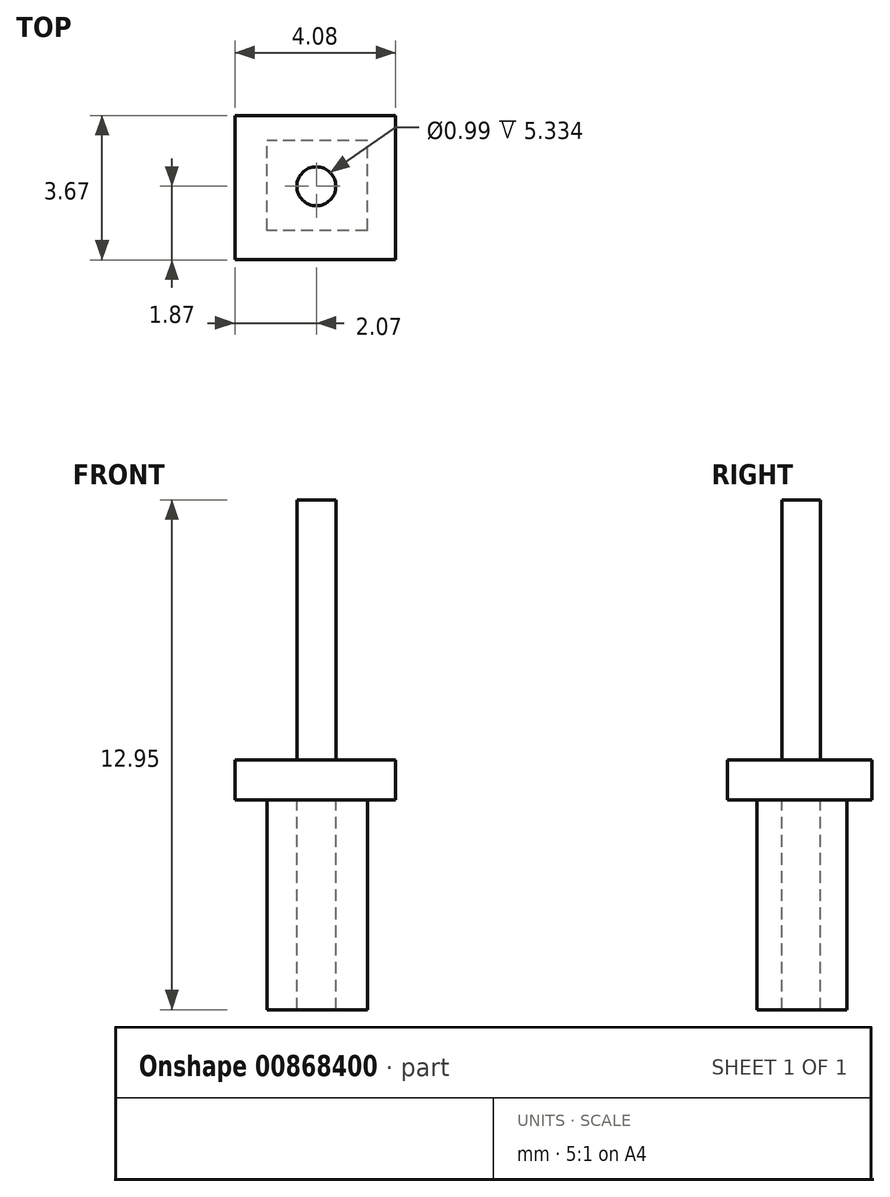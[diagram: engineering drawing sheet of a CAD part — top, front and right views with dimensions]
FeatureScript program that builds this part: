
annotation { "Feature Type Name" : "Feature", "Feature Type Description" : "" }
export const myFeature = defineFeature(function(context is Context, id is Id, definition is map)
    precondition{}
    {
        {
            var Q0;
            Q0=qCreatedBy(makeId("Top.planeOp"),FACE);
            var sketch = newSketch(context, id + "F0", { "sketchPlane" : qUnion([Q0])});
            skCircle(sketch, "E0", {"center": v(0, 0) * mm, "radius": 0.5 * mm});
            skLineSegment(sketch, "E1.bottom", {"start": v(-1.25, 1.16) * mm, "end": v(1.3, 1.16) * mm});
            skLineSegment(sketch, "E1.top", {"start": v(-1.25, -1.12) * mm, "end": v(1.3, -1.12) * mm});
            skLineSegment(sketch, "E1.left", {"start": v(-1.25, 1.16) * mm, "end": v(-1.25, -1.12) * mm});
            skLineSegment(sketch, "E1.right", {"start": v(1.3, 1.16) * mm, "end": v(1.3, -1.12) * mm});
            skSolve(sketch);
        }
        {
            var Q0;
            Q0=qCreatedBy(makeId("Top.planeOp"),FACE);
            var sketch = newSketch(context, id + "F1", { "sketchPlane" : qUnion([Q0])});
            skLineSegment(sketch, "E2.bottom", {"start": v(-2.07, 1.8) * mm, "end": v(2, 1.8) * mm});
            skLineSegment(sketch, "E2.top", {"start": v(-2.07, -1.87) * mm, "end": v(2, -1.87) * mm});
            skLineSegment(sketch, "E2.left", {"start": v(-2.07, 1.8) * mm, "end": v(-2.07, -1.87) * mm});
            skLineSegment(sketch, "E2.right", {"start": v(2, 1.8) * mm, "end": v(2, -1.87) * mm});
            skSolve(sketch);
        }
        {
            var Q0;
            Q0=makeQuery(id+"F0.imprint","IMPRINT",FACE,{"disambiguationData":[TD([[makeQuery(id+"F0.imprint","IMPRINT",EDGE,{"derivedFrom":sQuery(id+"F0.wireOp",EDGE,"E0")}),-1.0]])]});
            extrude(context, id + "F2", {"entities" : qUnion([Q0]), "oppositeDirection" : true, "depth" : 6.35 * mm, "offsetDistance" : 25.4 * mm});
        }
        {
            var Q0;
            Q0=makeQuery(id+"F1.imprint","IMPRINT",FACE,{"disambiguationData":[TD([[makeQuery(id+"F1.imprint","IMPRINT",EDGE,{"derivedFrom":sQuery(id+"F1.wireOp",EDGE,"E2.bottom")}),-1.0]])]});
            extrude(context, id + "F3", {"entities" : qUnion([Q0]), "operationType" : NewBodyOperationType.ADD, "oppositeDirection" : true, "depth" : 1.02 * mm, "offsetDistance" : 25.4 * mm});
        }
        {
            var Q0;
            Q0=makeQuery(id+"F3.boolean.opBoolean","SPLIT",FACE,{"disambiguationData":[TD([makeQuery(id+"F2.opExtrude","SWEPT_FACE",FACE,{"disambiguationData":[OSD([sQuery(id+"F0.wireOp",EDGE,"E0")])]})])],"derivedFrom":makeQuery(id+"F3.opExtrude","CAP_FACE",FACE,{"disambiguationData":[OSD([sQuery(id+"F1.wireOp",EDGE,"E2.bottom"),sQuery(id+"F1.wireOp",EDGE,"E2.top"),sQuery(id+"F1.wireOp",EDGE,"E2.left"),sQuery(id+"F1.wireOp",EDGE,"E2.right")])],"isStart":false})});
            extrude(context, id + "F4", {"entities" : qUnion([Q0]), "operationType" : NewBodyOperationType.ADD, "oppositeDirection" : true, "depth" : 7.62 * mm, "offsetDistance" : 25.4 * mm});
        }
    });
